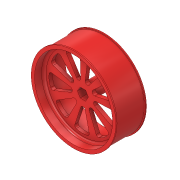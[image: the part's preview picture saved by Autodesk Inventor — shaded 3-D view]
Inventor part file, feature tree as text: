
AUTODESK INVENTOR PART (.ipt)
format: ipt  version: 2019.4 (Build 234330000, 330)  size: 802,304 bytes
history: native  units: in
note: dims shown in document units (in); Inventor stores cm internally (conversion verified against a paired STEP export)
features: extrude x7, fillet x7, sketch x7, pattern_circular x2, chamfer x2, plane x1, mirror x1, projected_geometry x1
ambient origin geometry x8: Origin, YZ Plane, XZ Plane, XY Plane, X Axis, Y Axis, Z Axis, Center Point
bodies: Solid1 (feature_tree)
feature tree (28):
  extrude  "Extrusion1"  Depth=0.75in
  extrude  "Extrusion4"  Depth=0.125in
  extrude  "Extrusion5"  Depth=0.5in TaperAngle=0.0deg
  extrude  "Extrusion6"  Depth=0.125in TaperAngle=0.0deg
  extrude  "Extrusion8"  Depth=0.1875in
  fillet  "Fillet1"  Radius=0.1875in
  pattern_circular  "Circular Pattern1"  [2 undecoded]
  fillet  "Fillet2"  Radius=0.938in
  extrude  "Extrusion9"  Depth=0.125in
  plane  "Work Plane1"
  mirror  "Mirror1"
  fillet  "Fillet3"  Radius=3.5433in
  fillet  "Fillet4"  Radius=0.13in
  fillet  "Fillet5"  Radius=4.5in
  extrude  "Extrusion10"  Depth=0.0625in TaperAngle=0.0deg
  pattern_circular  "Circular Pattern2"  [2 undecoded]
  fillet  "Fillet7"  Radius=0.125in
  fillet  "Fillet8"  Radius=0.125in
  chamfer  "Chamfer1"  Distance=0.125in
  chamfer  "Chamfer2"  Distance=0.125in
  sketch  "Sketch1"  dims[d0=4.4in d1=0.75in]
  sketch  "Sketch4"  dims[d2=0.504in d3=0.125in]
  sketch  "Sketch5"  dims[d9=1.625in d10=0.0in d24=0.5in d25=0.0in]
  sketch  "Sketch6"  dims[d26=0.75in d27=0.125in d28=0.0in]
  sketch  "Sketch7"  dims[d30=0.938in d31=0.0in d41=0.1875in d42=0.1875in]
  sketch  "Sketch8"  dims[d43=1.3568in]
  sketch  "Sketch9"  dims[d44=1.4375in d45=0.1875in d46=0.938in d47=0.0in d48=0.13in d49=3.5433in d50=360.0deg d52=0.13in d53=4.5in d54=0.0625in d55=0.0in d56=0.125in d57=0.125in d58=0.125in d59=0.125in d60=0.125in d62=0.2in d63=0.25in d70=1.0in d71=0.0in d72=3.5433in d73=360.0deg d77=1.0in d78=1.0in d79=0.25in d80=0.25in d81=0.5241in d82=0.947in d83=1.6614in d84=1.0272in d85=0.7in d87=0.015in d88=0.015in d89=0.0156in d90=0.125in d91=45.0deg d92=0.0156in d93=0.125in d94=45.0deg]
  projected_geometry  "Projected Loop1"
note: 4 required parameter values undecoded (feature->parameter linkage not recoverable at this tier; creation-order binding heuristic only, values carry confidence <= 0.55)
